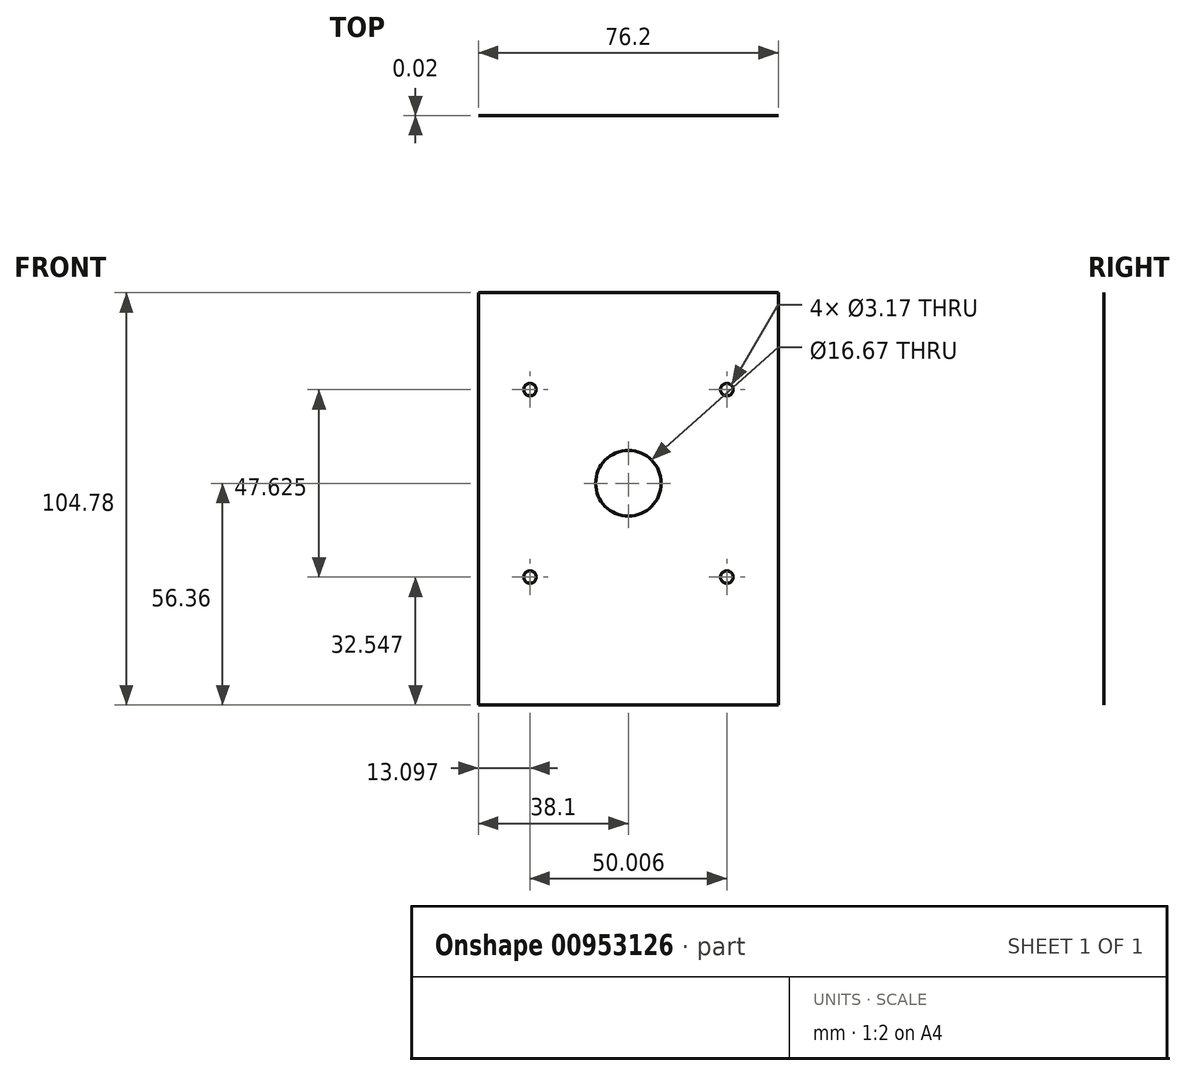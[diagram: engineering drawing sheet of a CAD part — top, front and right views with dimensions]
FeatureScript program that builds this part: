
annotation { "Feature Type Name" : "Feature", "Feature Type Description" : "" }
export const myFeature = defineFeature(function(context is Context, id is Id, definition is map)
    precondition{}
    {
        {
            var Q0;
            Q0=qCreatedBy(makeId("Front.planeOp"),FACE);
            var sketch = newSketch(context, id + "F0", { "sketchPlane" : qUnion([Q0])});
            skLineSegment(sketch, "E0.bottom", {"start": v(-38.1, 48.42) * mm, "end": v(38.1, 48.42) * mm});
            skLineSegment(sketch, "E0.top", {"start": v(-38.1, -56.36) * mm, "end": v(38.1, -56.36) * mm});
            skLineSegment(sketch, "E0.left", {"start": v(-38.1, 48.42) * mm, "end": v(-38.1, -56.36) * mm});
            skLineSegment(sketch, "E0.right", {"start": v(38.1, 48.42) * mm, "end": v(38.1, -56.36) * mm});
            skCircle(sketch, "E1", {"center": v(0, 0) * mm, "radius": 8.33 * mm});
            skCircle(sketch, "E2", {"center": v(-25, 23.81) * mm, "radius": 1.59 * mm});
            skCircle(sketch, "E3.0.1.0", {"center": v(-25, -23.81) * mm, "radius": 1.59 * mm});
            skCircle(sketch, "E3.1.0.0", {"center": v(25, 23.81) * mm, "radius": 1.59 * mm});
            skCircle(sketch, "E3.1.1.0", {"center": v(25, -23.81) * mm, "radius": 1.59 * mm});
            skLineSegment(sketch, "E3.direction1", {"start": v(-25, 23.81) * mm, "end": v(25, 23.81) * mm, "construction": true});
            skLineSegment(sketch, "E3.direction2", {"start": v(-25, 23.81) * mm, "end": v(-25, -23.81) * mm, "construction": true});
            skSolve(sketch);
        }
        {
            var Q0;
            Q0=makeQuery(id+"F0.imprint","IMPRINT",FACE,{"disambiguationData":[TD([[makeQuery(id+"F0.imprint","IMPRINT",EDGE,{"derivedFrom":sQuery(id+"F0.wireOp",EDGE,"E0.bottom")}),-1.0]])]});
            extrude(context, id + "F1", {"entities" : qUnion([Q0]), "depth" : 25 / 1625.6 * mm, "offsetDistance" : 25.4 * mm});
        }
    });
